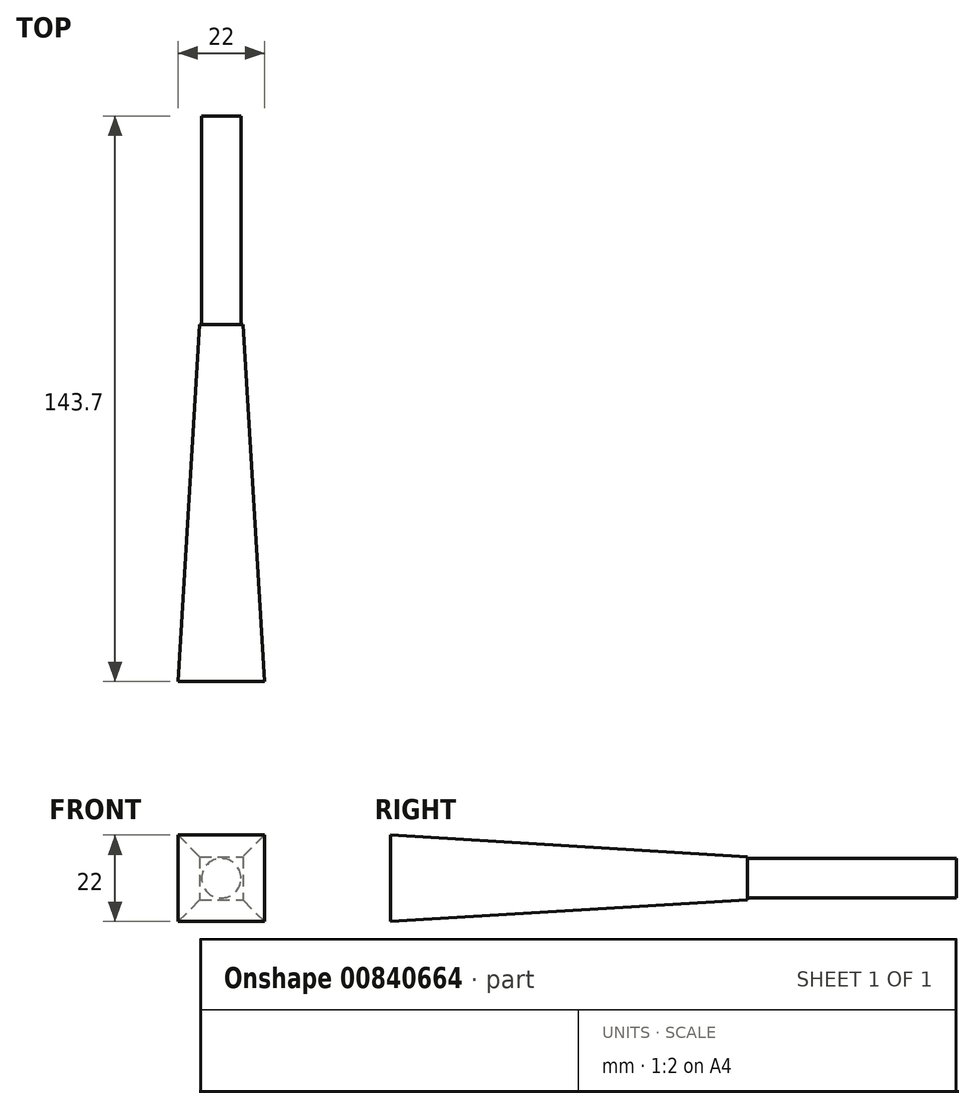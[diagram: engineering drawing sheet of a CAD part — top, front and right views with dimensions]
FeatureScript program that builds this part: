
annotation { "Feature Type Name" : "Feature", "Feature Type Description" : "" }
export const myFeature = defineFeature(function(context is Context, id is Id, definition is map)
    precondition{}
    {
        {
            var Q0;
            Q0=qCreatedBy(makeId("Front.planeOp"),FACE);
            var sketch = newSketch(context, id + "F0", { "sketchPlane" : qUnion([Q0])});
            skLineSegment(sketch, "E0.bottom", {"start": v(-11, 11) * mm, "end": v(11, 11) * mm});
            skLineSegment(sketch, "E0.top", {"start": v(-11, -11) * mm, "end": v(11, -11) * mm});
            skLineSegment(sketch, "E0.left", {"start": v(-11, 11) * mm, "end": v(-11, -11) * mm});
            skLineSegment(sketch, "E0.right", {"start": v(11, 11) * mm, "end": v(11, -11) * mm});
            skPoint(sketch, "E0.middle", {"position": v(0, 0) * mm});
            skSolve(sketch);
        }
        {
            var Q0;
            Q0=qCreatedBy(makeId("Front.planeOp"),FACE);
            cPlane(context, id + "F1", {"entities" : qUnion([Q0]), "cplaneType" : CPlaneType.OFFSET, "offset" : 90.7 * mm, "oppositeDirection" : true, "width" : 150 * mm, "height" : 150 * mm});
        }
        {
            var Q0;
            Q0=qCreatedBy(id+"F1.planeOp",FACE);
            var sketch = newSketch(context, id + "F2", { "sketchPlane" : qUnion([Q0])});
            skLineSegment(sketch, "E1.bottom", {"start": v(-5.5, 5.5) * mm, "end": v(5.5, 5.5) * mm});
            skLineSegment(sketch, "E1.top", {"start": v(-5.5, -5.5) * mm, "end": v(5.5, -5.5) * mm});
            skLineSegment(sketch, "E1.left", {"start": v(-5.5, 5.5) * mm, "end": v(-5.5, -5.5) * mm});
            skLineSegment(sketch, "E1.right", {"start": v(5.5, 5.5) * mm, "end": v(5.5, -5.5) * mm});
            skPoint(sketch, "E1.middle", {"position": v(0, 0) * mm});
            skSolve(sketch);
        }
        {
            var Q0;
            Q0=makeQuery(id+"F0.imprint","IMPRINT",FACE,{"disambiguationData":[TD([[makeQuery(id+"F0.imprint","IMPRINT",EDGE,{"derivedFrom":sQuery(id+"F0.wireOp",EDGE,"E0.bottom")}),-1.0]])]});
            var Q1;
            Q1=makeQuery(id+"F2.imprint","IMPRINT",FACE,{"disambiguationData":[TD([[makeQuery(id+"F2.imprint","IMPRINT",EDGE,{"derivedFrom":sQuery(id+"F2.wireOp",EDGE,"E1.bottom")}),-1.0]])]});
            loft(context, id + "F3", {"sheetProfilesArray" : [{ "sheetProfileEntities" : qUnion([Q0]) }, { "sheetProfileEntities" : qUnion([Q1]) }]});
        }
        {
            var Q0;
            Q0=makeQuery(id+"F3.opLoft","CAP_FACE",FACE,{"disambiguationData":[OSD([makeQuery(id+"F2.imprint","IMPRINT",FACE,{"disambiguationData":[TD([[makeQuery(id+"F2.imprint","IMPRINT",EDGE,{"derivedFrom":sQuery(id+"F2.wireOp",EDGE,"E1.bottom")}),-1.0]])]})])],"isStart":true});
            var sketch = newSketch(context, id + "F4", { "sketchPlane" : qUnion([Q0])});
            skCircle(sketch, "E2", {"center": v(0, 0) * mm, "radius": 5.01 * mm});
            skSolve(sketch);
        }
        {
            var Q0;
            Q0=makeQuery(id+"F4.imprint","IMPRINT",FACE,{"disambiguationData":[TD([[makeQuery(id+"F4.imprint","IMPRINT",EDGE,{"derivedFrom":sQuery(id+"F4.wireOp",EDGE,"E2")}),1.0]])]});
            extrude(context, id + "F5", {"entities" : qUnion([Q0]), "operationType" : NewBodyOperationType.ADD, "depth" : 53 * mm, "offsetDistance" : 25 * mm});
        }
    });
